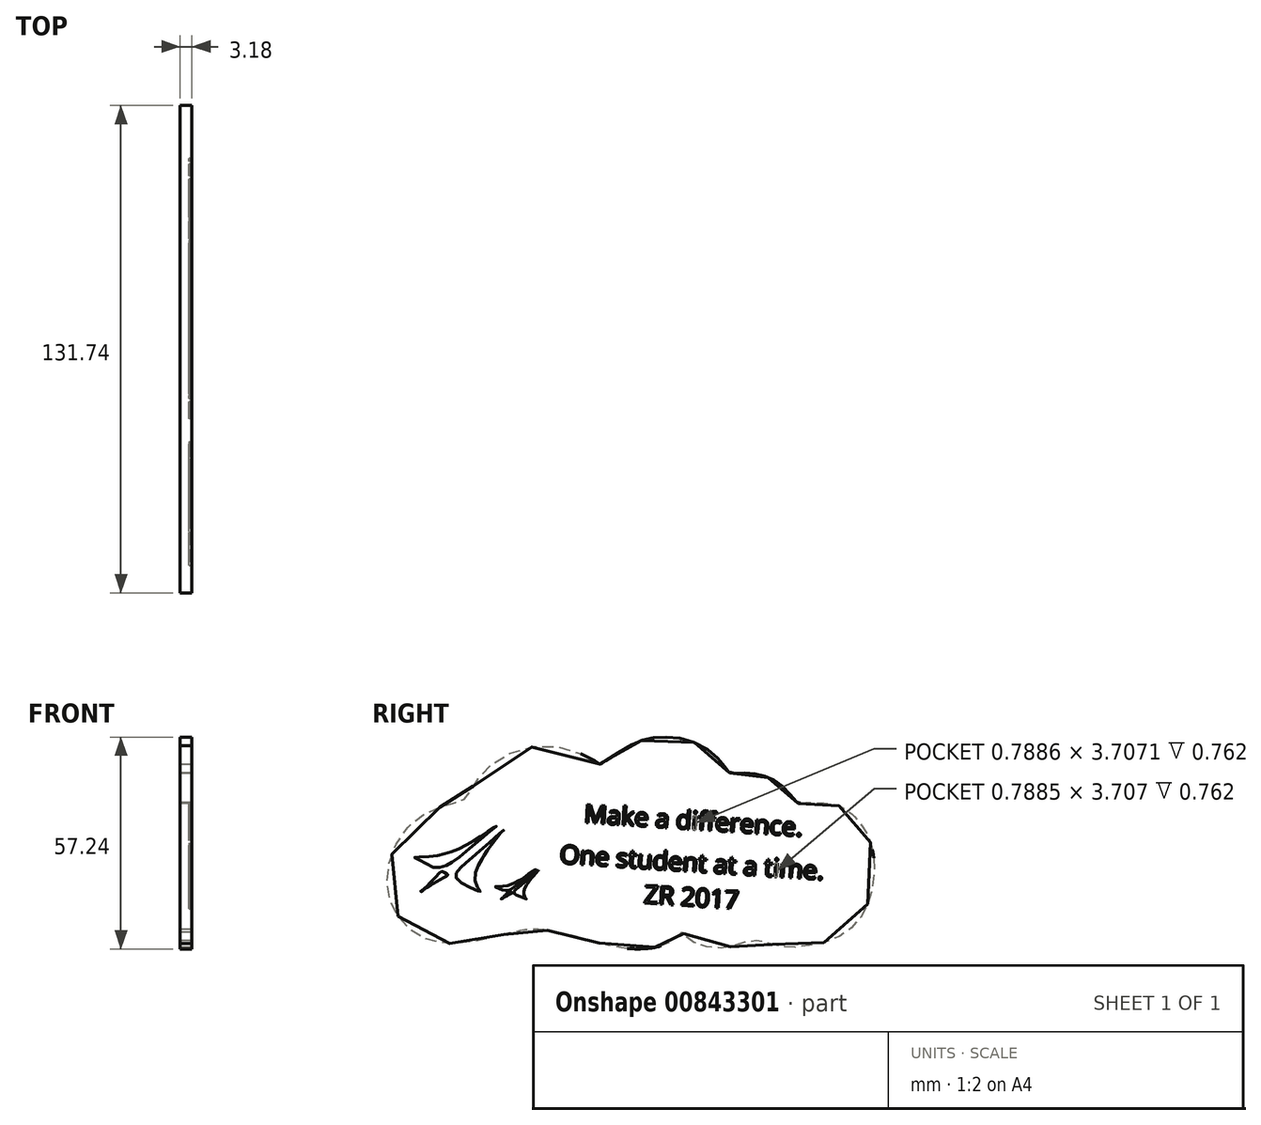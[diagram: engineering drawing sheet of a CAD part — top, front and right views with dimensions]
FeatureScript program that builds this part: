
annotation { "Feature Type Name" : "Feature", "Feature Type Description" : "" }
export const myFeature = defineFeature(function(context is Context, id is Id, definition is map)
    precondition{}
    {
        {
            var Q0;
            Q0=qCreatedBy(makeId("Right.planeOp"),FACE);
            var sketch = newSketch(context, id + "F0", { "sketchPlane" : qUnion([Q0])});
            skFitSpline(sketch, "E0", {"points": [v(-33.71, -20.96) * mm, v(-42.15, -22.85) * mm, v(-54, -22.39) * mm, v(-62.85, -15) * mm, v(-64.82, -2.45) * mm, v(-56.45, 10.84) * mm, v(-45.87, 15.02) * mm, v(-43.55, 16.44) * mm, v(-38.07, 24.14) * mm, v(-18.5, 29.75) * mm, v(-7.57, 25.06) * mm, v(-7.55, 25.06) * mm, v(0, 29.85) * mm, v(7.48, 32.29) * mm, v(18.1, 30.9) * mm, v(26, 24.69) * mm, v(27.5, 22.78) * mm, v(31.6, 22.78) * mm, v(37.42, 21.69) * mm, v(42.25, 18.63) * mm, v(45.87, 14.6) * mm, v(46.27, 14.6) * mm, v(52.7, 14.6) * mm, v(58.34, 13.18) * mm, v(63.75, 7.7) * mm, v(66.56, -2.4) * mm, v(63.43, -15.33) * mm, v(54.88, -22.42) * mm, v(42.8, -24.3) * mm, v(38.3, -23.37) * mm, v(33.38, -22.63) * mm, v(25.26, -24.6) * mm, v(16.1, -22) * mm, v(14.44, -20.34) * mm, v(12.58, -22) * mm, v(7.77, -24.3) * mm, v(-1.82, -24.5) * mm, v(-12.87, -21.8) * mm, v(-21.42, -19.92) * mm, v(-26, -19.5) * mm, v(-33.71, -20.96) * mm]});
            skSolve(sketch);
        }
        {
            var Q0;
            Q0 = qSketchRegion(id + "F0", true);
            extrude(context, id + "F1", {"entities" : qUnion([Q0]), "depth" : 3.17 * mm, "offsetDistance" : 25.4 * mm});
        }
        {
            var Q0;
            Q0=makeQuery(id+"F1.opExtrude","CAP_FACE",FACE,{"disambiguationData":[OSD([sQuery(id+"F0.wireOp",EDGE,"E0")])],"isStart":false});
            var sketch = newSketch(context, id + "F2", { "sketchPlane" : qUnion([Q0])});
            skFitSpline(sketch, "E1", {"points": [v(-49.21, -2.23) * mm, v(-52.14, -2.86) * mm, v(-55.73, -1.17) * mm, v(-57.75, -0.05) * mm, v(-54.33, 0.07) * mm, v(-49.96, 0.8) * mm, v(-46.6, 1.91) * mm, v(-41.85, 4.37) * mm, v(-38.22, 6.77) * mm, v(-35.65, 8.37) * mm, v(-36.8, 7.4) * mm, v(-45.75, 0) * mm, v(-49.21, -2.23) * mm]});
            skLineSegment(sketch, "E2", {"start": v(-54.05, -7.77) * mm, "end": v(-32.8, 9.36) * mm, "construction": true});
            skFitSpline(sketch, "E3", {"points": [v(-33.59, 7.42) * mm, v(-39.56, 2.12) * mm, v(-44.02, -1.76) * mm, v(-46.52, -4.31) * mm, v(-46.3, -5.96) * mm, v(-41.22, -8.84) * mm, v(-39.99, -9.33) * mm, v(-40.69, -8.29) * mm, v(-41.44, -4.8) * mm, v(-39.93, -1.13) * mm, v(-38.98, 0.42) * mm, v(-37.36, 2.79) * mm, v(-34.9, 6) * mm, v(-33.59, 7.42) * mm]});
            skFitSpline(sketch, "E4", {"points": [v(-50.56, -3.85) * mm, v(-50, -4.01) * mm, v(-49.23, -4.41) * mm, v(-48.78, -4.77) * mm, v(-49.48, -5.3) * mm, v(-51.74, -6.6) * mm, v(-54.18, -8.12) * mm, v(-56.15, -9.34) * mm, v(-55.15, -8.46) * mm, v(-53.35, -6.72) * mm, v(-51.96, -5.26) * mm, v(-51.05, -4.24) * mm, v(-50.56, -3.85) * mm]});
            skFitSpline(sketch, "E5", {"points": [v(-32.36, -9.02) * mm, v(-33.55, -8.96) * mm, v(-35.37, -8.27) * mm, v(-35.99, -7.95) * mm, v(-35.71, -7.93) * mm, v(-33.2, -7.79) * mm, v(-31.03, -7.11) * mm, v(-29.36, -6.26) * mm, v(-27.55, -5.1) * mm, v(-24.99, -3.36) * mm, v(-27.24, -5.21) * mm, v(-31.49, -8.6) * mm, v(-32.36, -9.02) * mm]});
            skLineSegment(sketch, "E6", {"start": v(-30.92, -8.6) * mm, "end": v(-15.44, 3.92) * mm, "construction": true});
            skFitSpline(sketch, "E7", {"points": [v(-24.3, -3.58) * mm, v(-24.84, -3.99) * mm, v(-27.65, -6.48) * mm, v(-29.52, -8.06) * mm, v(-30.38, -8.83) * mm, v(-30.92, -9.46) * mm, v(-30.67, -10.02) * mm, v(-29.43, -10.62) * mm, v(-27.52, -11.35) * mm, v(-27.76, -11.09) * mm, v(-28.24, -10.08) * mm, v(-28.18, -9.02) * mm, v(-27.42, -7.5) * mm, v(-26.34, -5.94) * mm, v(-24.96, -4.33) * mm, v(-24.3, -3.58) * mm]});
            skFitSpline(sketch, "E8", {"points": [v(-32.52, -9.6) * mm, v(-32.26, -9.38) * mm, v(-32.18, -9.37) * mm, v(-31.43, -9.66) * mm, v(-31.43, -9.7) * mm, v(-34.1, -11.25) * mm, v(-34.36, -11.4) * mm, v(-34.3, -11.3) * mm, v(-33.08, -10.12) * mm, v(-32.52, -9.6) * mm]});
            skSolve(sketch);
        }
        {
            var Q0;
            Q0 = qSketchRegion(id + "F2", true);
            extrude(context, id + "F3", {"entities" : qUnion([Q0]), "operationType" : NewBodyOperationType.REMOVE, "oppositeDirection" : true, "depth" : 0.76 * mm, "offsetDistance" : 25.4 * mm});
        }
        {
            var Q0;
            Q0=makeQuery(id+"F1.opExtrude","CAP_FACE",FACE,{"disambiguationData":[OSD([sQuery(id+"F0.wireOp",EDGE,"E0")])],"isStart":false});
            var sketch = newSketch(context, id + "F4", { "sketchPlane" : qUnion([Q0])});
            skText(sketch, "E9", { "text": "Make a difference.\n", "fontName": "OpenSans-Regular.ttf"});
            skText(sketch, "E10", { "text": "One student at a time.\n\n", "fontName": "OpenSans-Regular.ttf"});
            skText(sketch, "E11", { "text": "ZR 2017\n", "fontName": "OpenSans-Regular.ttf"});
            const initialGuessF4  = {"E9": [-0.01205, 0.00935, 0.998, -0.0631, 0.00495], "E10": [-0.01861, -0.00163, 0.998, -0.0631, 0.00495], "E11": [0.00414, -0.01244, 0.998, -0.0631, 0.00495]};
            skSetInitialGuess(sketch, initialGuessF4);
            skSolve(sketch);
        }
        {
            var Q0;
            Q0 = qSketchRegion(id + "F4", true);
            extrude(context, id + "F5", {"entities" : qUnion([Q0]), "operationType" : NewBodyOperationType.REMOVE, "oppositeDirection" : true, "depth" : 0.76 * mm, "offsetDistance" : 25.4 * mm});
        }
    });
